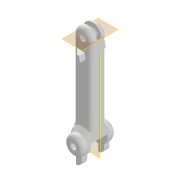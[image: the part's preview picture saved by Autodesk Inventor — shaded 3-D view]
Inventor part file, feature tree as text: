
AUTODESK INVENTOR PART (.ipt)
format: ipt  version: 2020.2 (Build 242310000, 310)  size: 321,024 bytes
history: native  units: mm
features: sketch x9, extrude x8, mirror x5, chamfer x3, fillet x3, plane x2, revolve x1
ambient origin geometry x8: Origin, YZ Plane, XZ Plane, XY Plane, X Axis, Y Axis, Z Axis, Center Point
bodies: Solid1 (feature_tree)
feature tree (31):
  extrude  "base"  Depth=48.0mm
  extrude  "joint"  Depth=10.0mm
  plane  "Work Plane1"
  mirror  "Mirror1"
  chamfer  "Chamfer1"  Distance=8.0mm
  extrude  "joint_2"  Depth=3.0mm
  fillet  "Fillet2"  Radius=5.0mm
  plane  "Work Plane2"
  revolve  "Revolution2"  [1 undecoded]
  extrude  "Extrusion8"  Depth=2.0mm TaperAngle=45.0deg
  extrude  "Extrusion9"  Depth=2.0mm
  mirror  "Mirror4"
  fillet  "Fillet4"  Radius=3.5mm
  extrude  "Extrusion10"  Depth=40.0mm TaperAngle=0.0deg
  mirror  "Mirror5"
  chamfer  "Chamfer3"  Distance=13.962634mm
  extrude  "lock_1"  Depth=2.0mm
  mirror  "Mirror2"
  chamfer  "Chamfer2"  Distance=3.0mm
  extrude  "lock_2"  Depth=3.0mm TaperAngle=45.0deg
  mirror  "Mirror3"
  fillet  "Fillet3"  Radius=4.0mm
  sketch  "Sketch1"  dims[d0=3.0mm d1=48.0mm]
  sketch  "Sketch2"  dims[d2=3.0mm d3=10.0mm]
  sketch  "Sketch4"  dims[d4=10.0mm d5=8.0mm d6=0.0mm]
  sketch  "Sketch7"  dims[d7=10.0mm d8=3.0mm d9=5.0mm d10=0.0mm]
  sketch  "Sketch8"  dims[d12=10.5mm d13=3.0mm]
  sketch  "Sketch9"  dims[d14=9.0mm d15=0.0mm d16=2.0mm d17=2.0mm d18=45.0deg]
  sketch  "Sketch10"  dims[d19=2.0mm d20=3.5mm d21=3.5mm]
  sketch  "Sketch11"  dims[d23=2.5mm d24=40.0mm d25=0.0mm]
  sketch  "Sketch12"  dims[d32=6.0mm d33=13.962634mm d34=5.0mm d35=3.0mm d36=0.0mm d37=3.0mm d38=2.0mm d39=45.0deg d40=4.0mm d41=3.0mm d42=3.0mm d43=0.0mm d44=3.0mm d45=4.0mm d46=90.0deg d47=3.5mm d48=2.5mm d49=180.0deg d50=5.0mm d51=0.0mm d52=4.0mm d53=3.0mm d54=3.0mm d55=0.0mm d56=3.0mm d57=6.0mm d58=3.0mm d59=13.962634mm d60=3.0mm d61=0.0mm d62=3.0mm d63=2.0mm d64=45.0deg]
note: 1 required parameter value undecoded (feature->parameter linkage not recoverable at this tier; creation-order binding heuristic only, values carry confidence <= 0.55)
